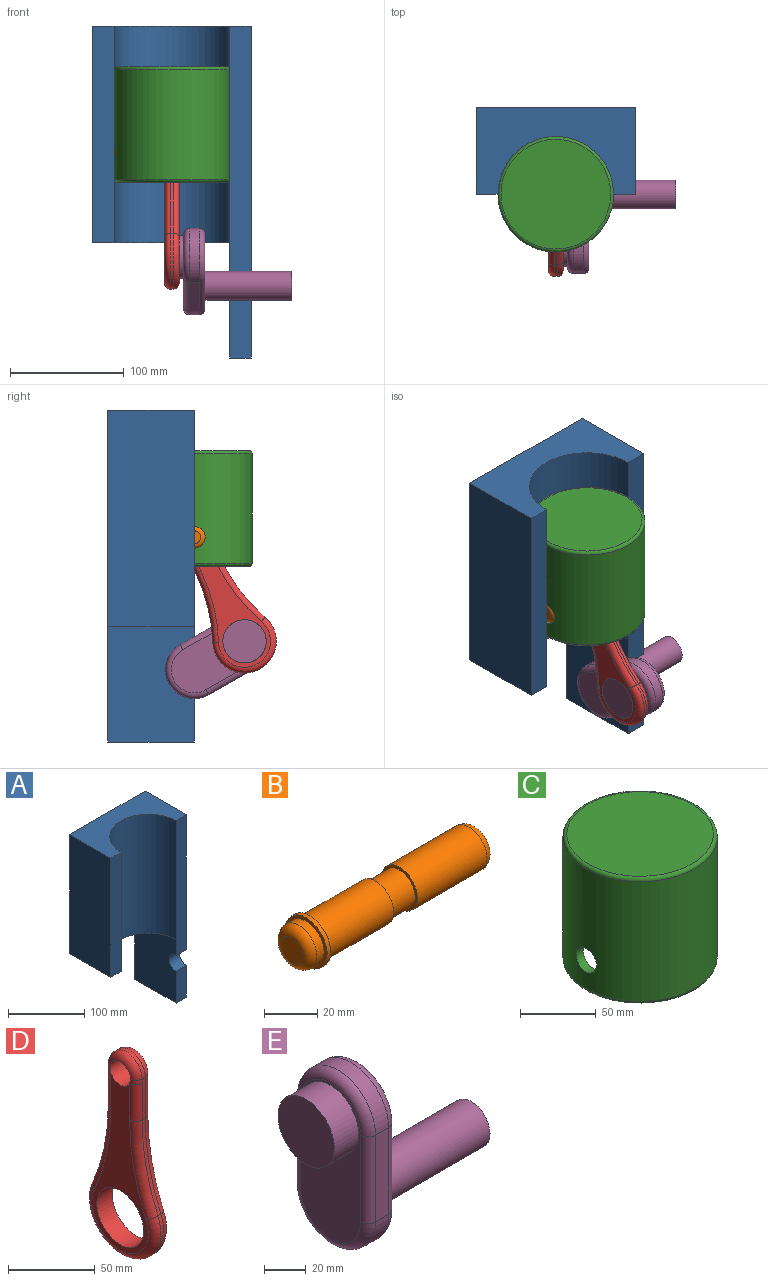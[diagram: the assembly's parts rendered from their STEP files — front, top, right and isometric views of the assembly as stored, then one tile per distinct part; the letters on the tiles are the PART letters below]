
ASSEMBLY  parts=5 mates=5
PART A: 12 faces, bbox 139.7x76.2x292.1 mm
  f0: plane 50.8x19.05mm, normal (0,-1,0), area 967.7mm2, adj f1,f2,f10,f11
  f1: plane 292.1x76.2mm, normal (1,0,0), area 22004.7mm2, adj f0,f4,f8,f9,f10,f11
  f2: plane 101.6x76.2mm, normal (-1,0,0), area 7488.6mm2, adj f0,f3,f4,f8,f10,f11
  f3: plane 120.65x76.2mm, normal (0,0,-1), area 5139.9mm2, adj f2,f4,f5,f6,f7
  f4: plane 292.1x139.7mm, normal (0,1,0), area 28548.3mm2, adj f1,f2,f3,f5,f9,f10
  f5: plane 190.5x76.2mm, normal (-1,0,0), area 14516.1mm2, adj f3,f4,f6,f9
  f6: plane 190.5x19.05mm, normal (0,-1,0), area 3629mm2, adj f3,f5,f7,f9
  f7: cylinder r=50.8mm len=190.5mm, axis (0,0,1), area 30402.4mm2, adj f3,f6,f8,f9
  f8: plane 215.9x19.05mm, normal (0,-1,0), area 4112.9mm2, adj f1,f2,f7,f9,f11
  f9: plane 139.7x76.2mm, normal (0,0,1), area 6591.5mm2, adj f1,f4,f5,f6,f7,f8
  f10: plane 76.2x19.05mm, normal (0,0,-1), area 1451.6mm2, adj f0,f1,f2,f4
  f11: cylinder r=12.7mm len=25.4mm, axis (1,0,0), area 760.1mm2, adj f0,f1,f2,f8
PART B: 16 faces, bbox 97.8x22.2x22.2 mm
  f0: cylinder r=9.53mm len=34.93mm, axis (-1,0,0), area 2090.2mm2, adj f1,f12
  f1: plane 19.05x19.05mm, normal (1,0,0), area 70.9mm2, adj f0,f2
  f2: cylinder r=8.26mm len=16.51mm, axis (-1,0,0), area 658.7mm2, adj f1,f3
  f3: plane 19.05x19.05mm, normal (-1,0,0), area 70.9mm2, adj f2,f4
  f4: cylinder r=9.53mm len=36.83mm, axis (-1,0,0), area 2204.2mm2, adj f3,f5
  f5: torus R=5.71mm, axis (-1,0,0), area 306.1mm2, adj f4,f6
  f6: plane 11.43x11.43mm, normal (1,0,0), area 102.6mm2, adj f5
  f7: plane 11.43x11.43mm, normal (-1,0,0), area 102.6mm2, adj f8
  f8: torus R=5.71mm, axis (-1,0,0), area 306.1mm2, adj f7,f9
  f9: cylinder r=9.53mm len=19.05mm, axis (-1,0,0), area 228mm2, adj f8,f10
  f10: plane 22.23x22.23mm, normal (-1,0,0), area 102.9mm2, adj f9,f11
  f11: cylinder r=11.11mm len=22.23mm, axis (-1,0,0), area 133mm2, adj f10,f12
  f12: plane 22.23x22.23mm, normal (1,0,0), area 102.9mm2, adj f0,f11
  f13: plane 2.54x2.54mm, normal (-1,0,0), area 5.1mm2, adj f14
  f14: cylinder r=1.27mm len=12.7mm, axis (-1,0,0), area 101.3mm2, adj f13,f15
  f15: plane 2.54x2.54mm, normal (1,0,0), area 5.1mm2, adj f14
PART C: 11 faces, bbox 110x110x101.6 mm
  f0: cylinder r=50.8mm len=101.6mm, axis (0,0,1), area 30520.2mm2, adj f7,f9,f10
  f1: cylinder r=44.45mm len=88.9mm, axis (0,0,-1), area 12906.2mm2, adj f4,f6,f7,f8
  f2: plane 96.52x96.52mm, normal (0,0,-1), area 380mm2, adj f8,f10
  f3: plane 96.52x96.52mm, normal (0,0,1), area 7316.9mm2, adj f9
  f4: plane 88.9x88.9mm, normal (0,0,-1), area 6207.2mm2, adj f1
  f5: plane 19.05x19.05mm, normal (-1,0,0), area 285mm2, adj f6
  f6: cylinder r=9.53mm len=19.05mm, axis (-1,0,0), area 182.8mm2, adj f1,f5
  f7: cylinder r=9.53mm len=19.05mm, axis (-1,0,0), area 384mm2, adj f0,f1
  f8: torus R=46.99mm, axis (0,0,1), area 1137.4mm2, adj f1,f2
  f9: torus R=48.26mm, axis (0,0,1), area 1250.4mm2, adj f0,f3
  f10: torus R=48.26mm, axis (0,0,1), area 1250.4mm2, adj f0,f2
PART D: 26 faces, bbox 13.9x60.5x145.6 mm
  f0: cylinder r=12.7mm len=25.4mm, axis (-1,0,0), area 104.5mm2, adj f1,f5,f17,f23
  f1: plane 29.21x2.62mm, normal (0,-1,0), area 74.3mm2, adj f0,f2,f13,f15,f19,f21
  f2: cylinder r=151.61mm len=61.13mm, axis (-1,0,0), area 159.8mm2, adj f1,f3,f11,f18
  f3: cylinder r=27.94mm len=55.88mm, axis (-1,0,0), area 281.9mm2, adj f2,f4,f10,f20
  f4: cylinder r=151.61mm len=61.13mm, axis (-1,0,0), area 159.8mm2, adj f3,f5,f12,f22
  f5: plane 29.21x2.62mm, normal (0,1,0), area 74.3mm2, adj f0,f4,f14,f16,f24,f25
  f6: cylinder r=8.26mm len=16.51mm, axis (-1,0,0), area 658.7mm2, adj f8,f9,f15,f16,f17,f21,f23,f25
  f7: cylinder r=19.05mm len=38.1mm, axis (-1,0,0), area 1520.1mm2, adj f8,f9
  f8: plane 121.29x45.72mm, normal (1,0,0), area 1944.3mm2, adj f6,f7,f18,f19,f20,f22,f24
  f9: plane 121.29x45.72mm, normal (-1,0,0), area 1944.3mm2, adj f6,f7,f10,f11,f12,f13,f14
  f10: torus R=22.86mm, axis (1,0,0), area 827mm2, adj f3,f9,f11,f12
  f11: torus R=156.69mm, axis (1,0,0), area 508.2mm2, adj f2,f9,f10,f13
  f12: torus R=156.69mm, axis (1,0,0), area 508.2mm2, adj f4,f9,f10,f14
  f13: cylinder r=5.08mm len=26.03mm, axis (0,0,-1), area 207.7mm2, adj f1,f9,f11,f15
  f14: cylinder r=5.08mm len=26.03mm, axis (0,0,1), area 207.7mm2, adj f5,f9,f12,f16
  f15: bspline ~5.72x5.7mm, area 24mm2, adj f1,f6,f13,f17
  f16: bspline ~5.72x5.7mm, area 24mm2, adj f5,f6,f14,f17
  f17: torus R=7.62mm, axis (-1,0,0), area 256.2mm2, adj f0,f6,f15,f16
  f18: torus R=156.69mm, axis (1,0,0), area 508.2mm2, adj f2,f8,f19,f20
  f19: cylinder r=5.08mm len=26.03mm, axis (0,0,1), area 207.7mm2, adj f1,f8,f18,f21
  f20: torus R=22.86mm, axis (1,0,0), area 827mm2, adj f3,f8,f18,f22
  f21: bspline ~5.72x5.7mm, area 24mm2, adj f1,f6,f19,f23
  f22: torus R=156.69mm, axis (1,0,0), area 508.2mm2, adj f4,f8,f20,f24
  f23: torus R=7.62mm, axis (1,0,0), area 256.2mm2, adj f0,f6,f21,f25
  f24: cylinder r=5.08mm len=26.03mm, axis (0,0,-1), area 207.7mm2, adj f5,f8,f22,f25
  f25: bspline ~5.72x5.7mm, area 24mm2, adj f5,f6,f23,f24
PART E: 18 faces, bbox 111.8x55x105.8 mm
  f0: cylinder r=19.05mm len=38.1mm, axis (1,0,0), area 1976.2mm2, adj f1,f7
  f1: plane 38.1x38.1mm, normal (-1,0,0), area 1140.1mm2, adj f0
  f2: plane 50.8x8.89mm, normal (0,1,0), area 451.6mm2, adj f3,f5,f13,f17
  f3: cylinder r=25.4mm len=50.8mm, axis (-1,0,0), area 709.4mm2, adj f2,f4,f11,f15
  f4: plane 50.8x8.89mm, normal (0,-1,0), area 451.6mm2, adj f3,f5,f10,f14
  f5: cylinder r=25.4mm len=50.8mm, axis (-1,0,0), area 709.4mm2, adj f2,f4,f12,f16
  f6: plane 91.44x40.64mm, normal (1,0,0), area 2855mm2, adj f8,f14,f15,f16,f17
  f7: plane 91.44x40.64mm, normal (-1,0,0), area 2221.6mm2, adj f0,f10,f11,f12,f13
  f8: cylinder r=12.7mm len=76.2mm, axis (-1,0,0), area 6080.5mm2, adj f6,f9
  f9: plane 25.4x25.4mm, normal (1,0,0), area 506.7mm2, adj f8
  f10: cylinder r=5.08mm len=50.8mm, axis (0,0,-1), area 405.4mm2, adj f4,f7,f11,f12
  f11: torus R=20.32mm, axis (1,0,0), area 590.5mm2, adj f3,f7,f10,f13
  f12: torus R=20.32mm, axis (1,0,0), area 590.5mm2, adj f5,f7,f10,f13
  f13: cylinder r=5.08mm len=50.8mm, axis (0,0,1), area 405.4mm2, adj f2,f7,f11,f12
  f14: cylinder r=5.08mm len=50.8mm, axis (0,0,1), area 405.4mm2, adj f4,f6,f15,f16
  f15: torus R=20.32mm, axis (1,0,0), area 590.5mm2, adj f3,f6,f14,f17
  f16: torus R=20.32mm, axis (1,0,0), area 590.5mm2, adj f5,f6,f14,f17
  f17: cylinder r=5.08mm len=50.8mm, axis (0,0,-1), area 405.4mm2, adj f2,f6,f15,f16
PLACE A at identity fixed
PLACE B t=(0,0,-35.83)mm
PLACE C t=(0,0,-35.83)mm
PLACE D rot(axis=(-1,0,0),25.8deg) t=(0,25.55,-76.55)mm
PLACE E rot(axis=(1,0,0),60.4deg) t=(0,-237.39,-49.49)mm
MATE revolute D.f0 <-> B.f0  axis (1,0,0) through (76.2,-76.2,-112.03)mm
MATE slider C.f0 <-> A.f7  axis (0,0,1) through (69.85,-76.2,-86.63)mm
MATE revolute A.f11 <-> E.f5  axis (-1,0,0) through (120.65,-76.2,-228.6)mm
MATE revolute E.f0 <-> D.f3  axis (-1,0,0) through (63.5,-120.38,-203.52)mm
MATE fastened B.f0 <-> C.f6  axis (1,0,0) through (116.84,-76.2,-112.03)mm
